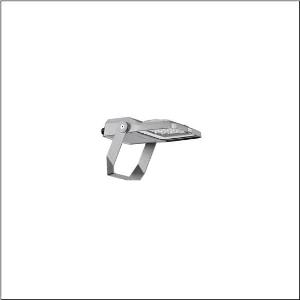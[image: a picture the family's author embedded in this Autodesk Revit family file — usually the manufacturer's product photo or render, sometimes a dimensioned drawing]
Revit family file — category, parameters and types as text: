
# Revit family: floodlight_fl_21_iq_micro___rs12_5xa7761a4b1a_38e5
name_source: partatom
category: Lighting Fixtures
units: mm (PartAtom-declared; Revit-internal decimal feet)

## family parameters
Cut with Voids When Loaded = No
Host = Face
Light Source = No
Part Type = Normal
Room Calculation Point = No
Round Connector Dimension = Use Diameter
Shared = No

## types (1)
- --- (1 x LED, 3220 lm, 23.1 W, 4000K)
    Apparent Load = 23 VA
    CIE Flux Codes = 79 92 99 100 100
    Color Rendering = 70
    Color Temperature = 4000K
    Default Elevation = 1800 mm
    Description = Floodlight FL 21 iQ micro, floodlight, primary light control with lens, of PMMA, primary optical cover: protective disc, of toughened safety glass, transparent, light distribution: RS12, light emission: direct distribution, installation type: surface-mounted, LED, High Power LED, rated luminous flux: 3.220lm, luminous efficacy: 139lm/W, light colour: 740, colour temperature: 4000K, control: optimised constant luminous flux control (CLO 2.0), Desk-Remote (wireless, voltage-free reading and setting of iQ features in the workshop via application-optimized NFC function/RFID function), Light-Fading, Smart-Wire, Night-Set, Lumen-Switch, Temp-Guard, Auto-Match, with terminal, 6-pole, mains connection: 220..240V, AC, 50/60Hz, start of lifetime: 23W, end of service life: 24W, reduction: 11W, luminaire housing, of diecast aluminium, powder-coated, Siteco® metallic grey (DB 702S), corrosivity category C5 mid according to DIN EN ISO 12944, sealing non-destructively replaceable, mounting bracket, of steel, galvanised, powder-coated, Siteco® metallic grey (DB 702S), protection rating (complete): IP66, insulation class (complete): insulation class II (safety insulation), certification: CE, ENEC, VDE, protection symbol: D, impact resistance: IK07, permissible operating ambient temperature: -40..+40°C, permissible operating ambient temperature for outdoor applications: -40..+50°C, standard: DIN EN 12944, LABS conformity tested according to VDMA 24364:2018-05, packaging unit: 1 piece

Light Distribution: RS12
    Height = 65 mm
    Lamp = 1 x LED
    Lamp Light Flux = 3220 lm
    Lamp Power = 23.1 W
    Lamp count = 1
    Length = 312 mm
    Luminous efficacy = 139 lm/W
    Manufacturer = Siteco
    ModVariant = No
    Model = 5XA7761A4B1A
    Mounting Place = Wall
    Mounting Type = Surface mounted
    Number of Poles = 1
    OnlyDefault = Yes
    Power Factor = 1
    Product Name = Floodlight FL 21 iQ micro | RS12
    Product group = floodlight | wall mounted
    ProductGroupID = 2001
    Protection Class = Protection class II
    Protection Degree = IP 66
    RLX_Detail_Level = 1
    RLX_Emergency_Light_Flux = 0 lm
    RLX_Emergency_Type = 0
    RLX_Emergency_Type_DB = No
    RlxData = <blob elided: 75061 chars, md5=800120aa>
    Socket = socket
    Standby Power = 0 W
    System Light Flux = 3220 lm
    System Power = 23 W
    Type Comments = factory setting: luminous flux: 100 % | dim-lin: 254 | 455 mA
    Type Image = l_1006880.jpg
    URL = http://relux.com
    VarID = @adj_153439
    Voltage = 0 V
    Weight = 0.00 kg
    Width = 230 mm

## geometry (parser evidence)
native form markers: Blend x4, Sweep x13
no freeform markers — native parametric forms only
